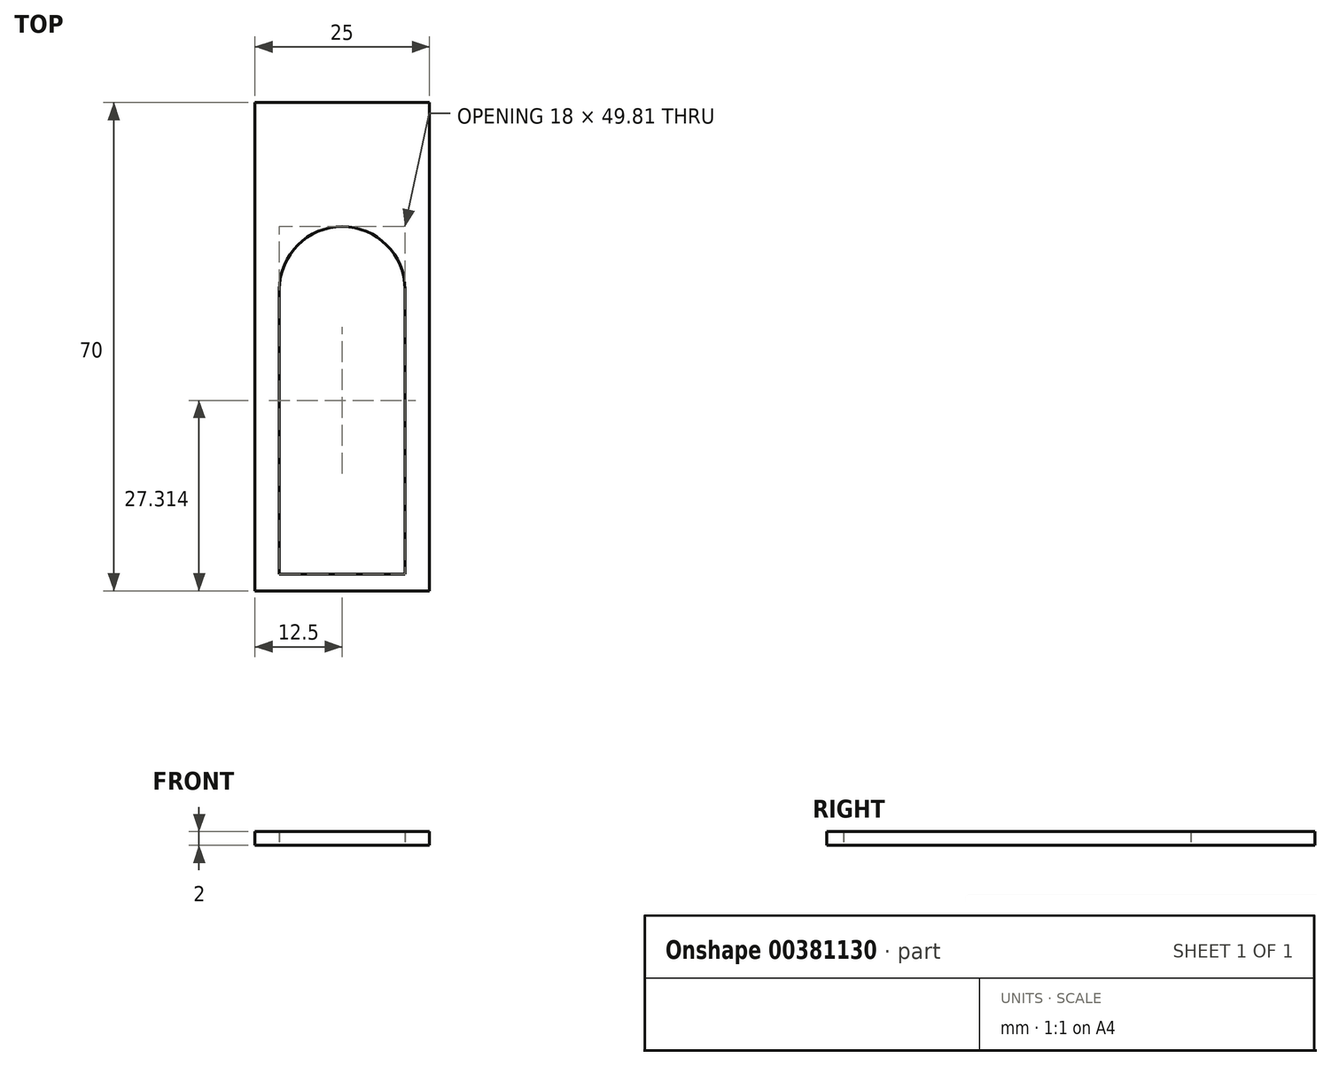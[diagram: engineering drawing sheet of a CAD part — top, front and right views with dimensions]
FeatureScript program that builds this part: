
annotation { "Feature Type Name" : "Feature", "Feature Type Description" : "" }
export const myFeature = defineFeature(function(context is Context, id is Id, definition is map)
    precondition{}
    {
        {
            var Q0;
            Q0=qCreatedBy(makeId("Top.planeOp"),FACE);
            var sketch = newSketch(context, id + "F0", { "sketchPlane" : qUnion([Q0])});
            skLineSegment(sketch, "E0.bottom", {"start": v(12.5, -35) * mm, "end": v(-12.5, -35) * mm});
            skLineSegment(sketch, "E0.top", {"start": v(12.5, 35) * mm, "end": v(-12.5, 35) * mm});
            skLineSegment(sketch, "E0.left", {"start": v(12.5, -35) * mm, "end": v(12.5, 35) * mm});
            skLineSegment(sketch, "E0.right", {"start": v(-12.5, -35) * mm, "end": v(-12.5, 35) * mm});
            skPoint(sketch, "E0.middle", {"position": v(0, 0) * mm});
            skLineSegment(sketch, "E1.bottom", {"start": v(-9, -32.6) * mm, "end": v(9, -32.6) * mm});
            skLineSegment(sketch, "E1.left", {"start": v(-9, -32.6) * mm, "end": v(-9, 8.22) * mm});
            skLineSegment(sketch, "E1.right", {"start": v(9, -32.6) * mm, "end": v(9, 8.22) * mm});
            skArc(sketch, "E2", {"start": v(9, 8.22) * mm, "mid": v(0.5, 17.2) * mm, "end": v(-8.94, 9.23) * mm});
            skArc(sketch, "E3", {"start": v(-8.94, 9.23) * mm, "mid": v(-8.99, 8.72) * mm, "end": v(-9, 8.22) * mm});
            skSolve(sketch);
        }
        {
            var Q0;
            Q0 = qSketchRegion(id + "F0", true);
            var Q1;
            Q1=makeQuery(id+"F0.imprint","IMPRINT",FACE,{"disambiguationData":[TD([[makeQuery(id+"F0.imprint","IMPRINT",EDGE,{"derivedFrom":sQuery(id+"F0.wireOp",EDGE,"E0.bottom")}),-1.0]])]});
            extrude(context, id + "F1", {"entities" : qUnion([Q0, Q1]), "depth" : 2 * mm});
        }
    });
